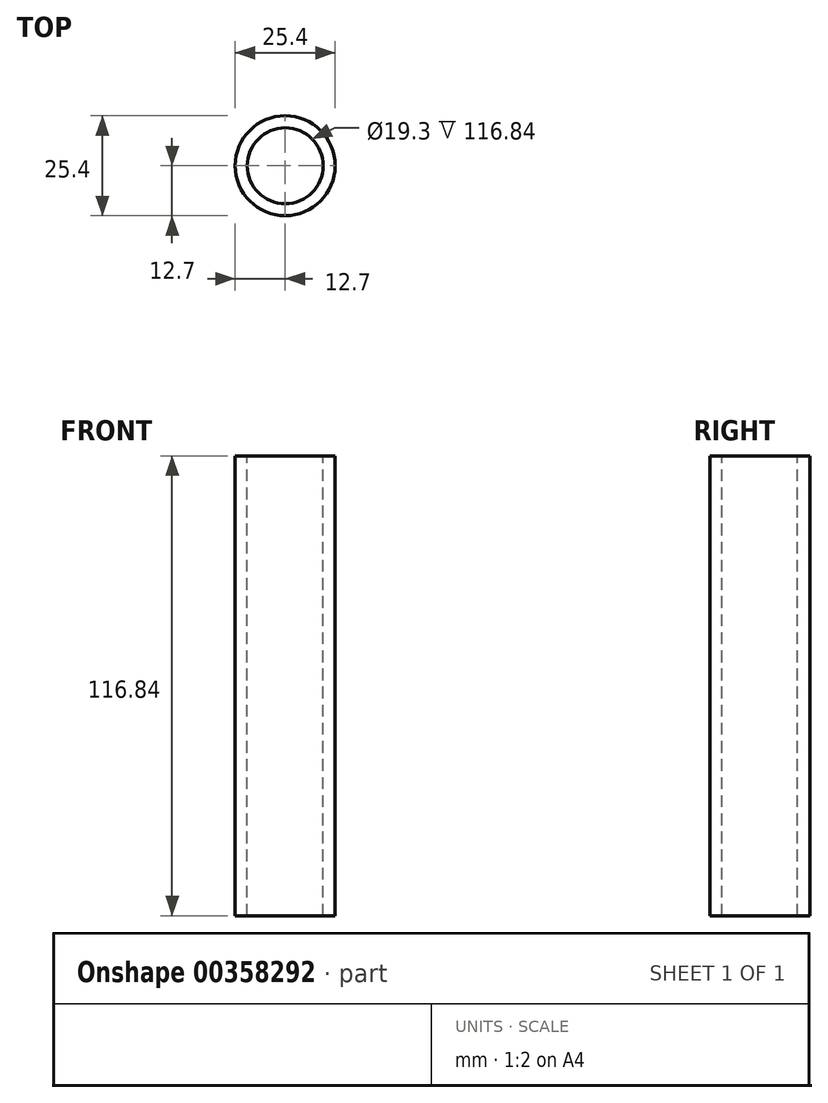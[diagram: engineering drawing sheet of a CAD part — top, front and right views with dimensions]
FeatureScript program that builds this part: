
annotation { "Feature Type Name" : "Feature", "Feature Type Description" : "" }
export const myFeature = defineFeature(function(context is Context, id is Id, definition is map)
    precondition{}
    {
        {
            var Q0;
            Q0=qCreatedBy(makeId("Top.planeOp"),FACE);
            var sketch = newSketch(context, id + "F0", { "sketchPlane" : qUnion([Q0])});
            skCircle(sketch, "E0", {"center": v(0, 0) * mm, "radius": 12.7 * mm});
            skSolve(sketch);
        }
        {
            var Q0;
            Q0 = qSketchRegion(id + "F0", true);
            extrude(context, id + "F1", {"entities" : qUnion([Q0]), "depth" : 116.84 * mm, "offsetDistance" : 25.4 * mm});
        }
        {
            var Q0;
            Q0=makeQuery(id+"F1.opExtrude","CAP_FACE",FACE,{"disambiguationData":[OSD([sQuery(id+"F0.wireOp",EDGE,"E0")])],"isStart":false});
            var sketch = newSketch(context, id + "F2", { "sketchPlane" : qUnion([Q0])});
            skCircle(sketch, "E1", {"center": v(0, 0) * mm, "radius": 9.65 * mm});
            skSolve(sketch);
        }
        {
            var Q0;
            Q0 = qSketchRegion(id + "F2", true);
            extrude(context, id + "F3", {"entities" : qUnion([Q0]), "operationType" : NewBodyOperationType.REMOVE, "endBound" : BoundingType.THROUGH_ALL, "oppositeDirection" : true, "depth" : 114.3 * mm, "offsetDistance" : 25.4 * mm});
        }
    });
